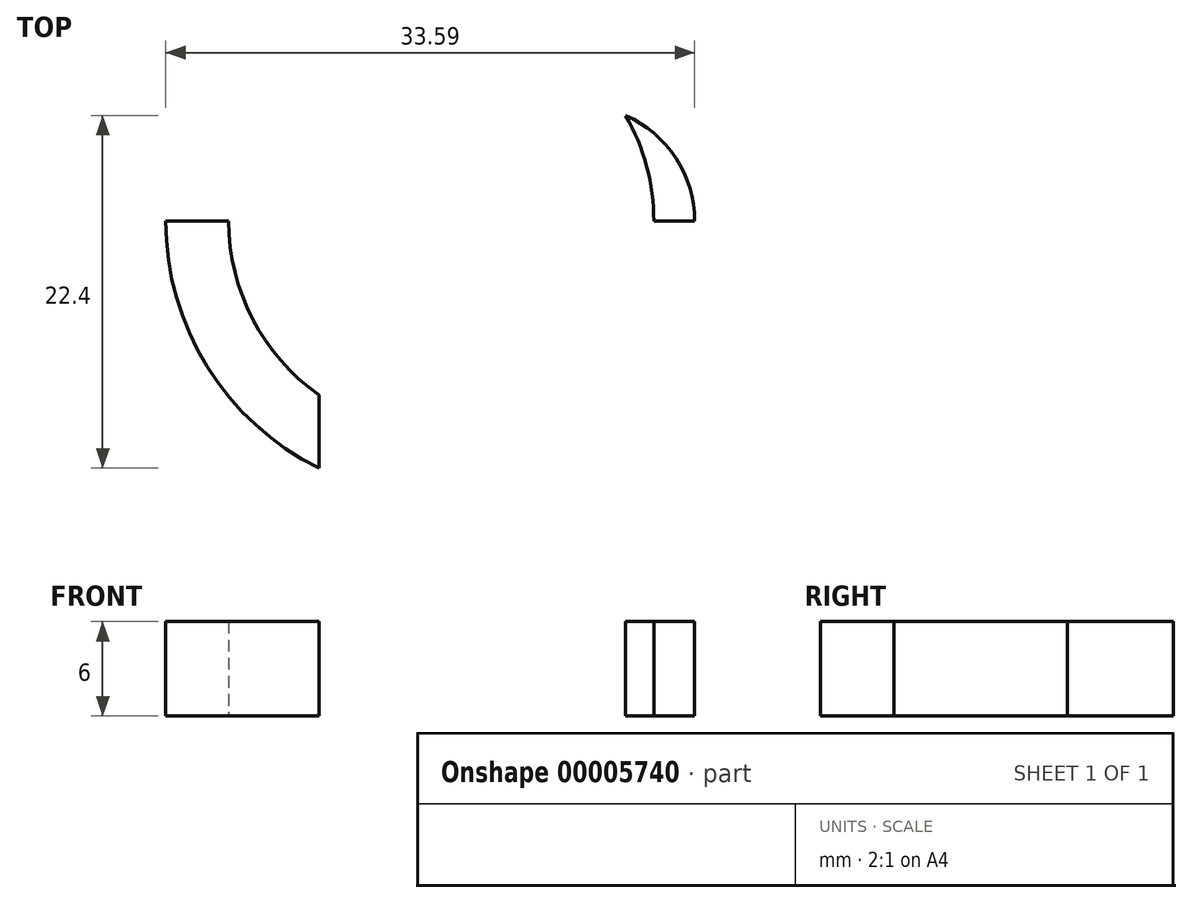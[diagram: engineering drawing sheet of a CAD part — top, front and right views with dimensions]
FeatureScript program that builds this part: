
annotation { "Feature Type Name" : "Feature", "Feature Type Description" : "" }
export const myFeature = defineFeature(function(context is Context, id is Id, definition is map)
    precondition{}
    {
        {
            var Q0;
            Q0=qCreatedBy(makeId("Top.planeOp"),FACE);
            var sketch = newSketch(context, id + "F0", { "sketchPlane" : qUnion([Q0])});
            skCircle(sketch, "E0", {"center": v(0, 0) * mm, "radius": 13.5 * mm});
            skCircle(sketch, "E1.0", {"center": v(0, 0) * mm, "radius": 17.5 * mm});
            skLineSegment(sketch, "E2", {"start": v(-7.78, -15.68) * mm, "end": v(-7.78, 15.68) * mm});
            skLineSegment(sketch, "E3", {"start": v(0, 0) * mm, "end": v(-23.3, 0) * mm});
            skLineSegment(sketch, "E4", {"start": v(0, 0) * mm, "end": v(17.5, 0) * mm});
            skArc(sketch, "E5", {"start": v(11.7, -6.72) * mm, "mid": v(16.1, 0) * mm, "end": v(11.7, 6.72) * mm});
            skSolve(sketch);
        }
        {
            var Q0;
            {var subQ0=sQuery(id+"F0.wireOp",EDGE,"E2");var subQ1=sQuery(id+"F0.wireOp",EDGE,"E0");var subQ2=makeQuery(id+"F0.imprint","INTERSECT",VERTEX,{"disambiguationData":[OD(0.0)],"derivedFrom":[subQ1,subQ0]});Q0=makeQuery(id+"F0.imprint","IMPRINT",FACE,{"disambiguationData":[TD([[makeQuery(id+"F0.imprint","IMPRINT",EDGE,{"disambiguationData":[TD([[subQ2,1.0]])],"derivedFrom":subQ1}),-1.0]])]});}
            var Q1;
            {var subQ0=sQuery(id+"F0.wireOp",EDGE,"E5");var subQ3=sQuery(id+"F0.wireOp",EDGE,"E0");var subQ4=makeQuery(id+"F0.imprint","INTERSECT",VERTEX,{"disambiguationData":[OD(0.0)],"derivedFrom":[subQ3,subQ0]});Q1=makeQuery(id+"F0.imprint","IMPRINT",FACE,{"disambiguationData":[TD([[makeQuery(id+"F0.imprint","IMPRINT",EDGE,{"disambiguationData":[TD([[subQ4,1.0]])],"derivedFrom":subQ3}),-1.0]])]});}
            extrude(context, id + "F1", {"entities" : qUnion([Q0, Q1]), "depth" : 6 * mm});
        }
        {
            var Q0;
            Q0 = qSketchRegion(id + "F0", true);
            var Q1;
            Q1=sQuery(id+"F0.wireOp",EDGE,"E3");
            extrude(context, id + "F2", {"entities" : qUnion([Q0]), "bodyType" : ToolBodyType.SURFACE, "surfaceEntities" : qUnion([Q1]), "depth" : 25 * mm});
        }
        {
            var Q0;
            Q0=makeQuery(id+"F2.opExtrude","SWEPT_FACE",FACE,{"disambiguationData":[OSD([sQuery(id+"F0.wireOp",EDGE,"E3")])]});
            var sketch = newSketch(context, id + "F3", { "sketchPlane" : qUnion([Q0])});
            skPoint(sketch, "E6.0", {"position": v(7.78, 6) * mm});
            skLineSegment(sketch, "E7.0", {"start": v(-11.7, 6) * mm, "end": v(7.78, 6) * mm});
            skLineSegment(sketch, "E8", {"start": v(0, 6) * mm, "end": v(0, 0) * mm});
            skCircle(sketch, "E9", {"center": v(0, 3) * mm, "radius": 1.5 * mm});
            skLineSegment(sketch, "E10", {"start": v(7.78, 6) * mm, "end": v(7.78, 0) * mm});
            skSolve(sketch);
        }
        {
            var Q0;
            {var subQ0=sQuery(id+"F3.wireOp",EDGE,"E9");var subQ1=sQuery(id+"F3.wireOp",EDGE,"E8");var subQ3=makeQuery(id+"F3.imprint","INTERSECT",VERTEX,{"disambiguationData":[OD(0.0)],"derivedFrom":[subQ1,subQ0]});Q0=makeQuery(id+"F3.imprint","IMPRINT",FACE,{"disambiguationData":[TD([[makeQuery(id+"F3.imprint","IMPRINT",EDGE,{"disambiguationData":[TD([[subQ3,-1.0]])],"derivedFrom":subQ1}),1.0]])]});}
            var Q1;
            {var subQ0=sQuery(id+"F3.wireOp",EDGE,"E9");var subQ1=sQuery(id+"F3.wireOp",EDGE,"E8");var subQ3=makeQuery(id+"F3.imprint","INTERSECT",VERTEX,{"disambiguationData":[OD(0.0)],"derivedFrom":[subQ1,subQ0]});Q1=makeQuery(id+"F3.imprint","IMPRINT",FACE,{"disambiguationData":[TD([[makeQuery(id+"F3.imprint","IMPRINT",EDGE,{"disambiguationData":[TD([[subQ3,-1.0]])],"derivedFrom":subQ1}),-1.0]])]});}
            extrude(context, id + "F4", {"entities" : qUnion([Q0, Q1]), "operationType" : NewBodyOperationType.REMOVE, "endBound" : BoundingType.SYMMETRIC, "oppositeDirection" : true, "depth" : 40 * mm});
        }
    });
